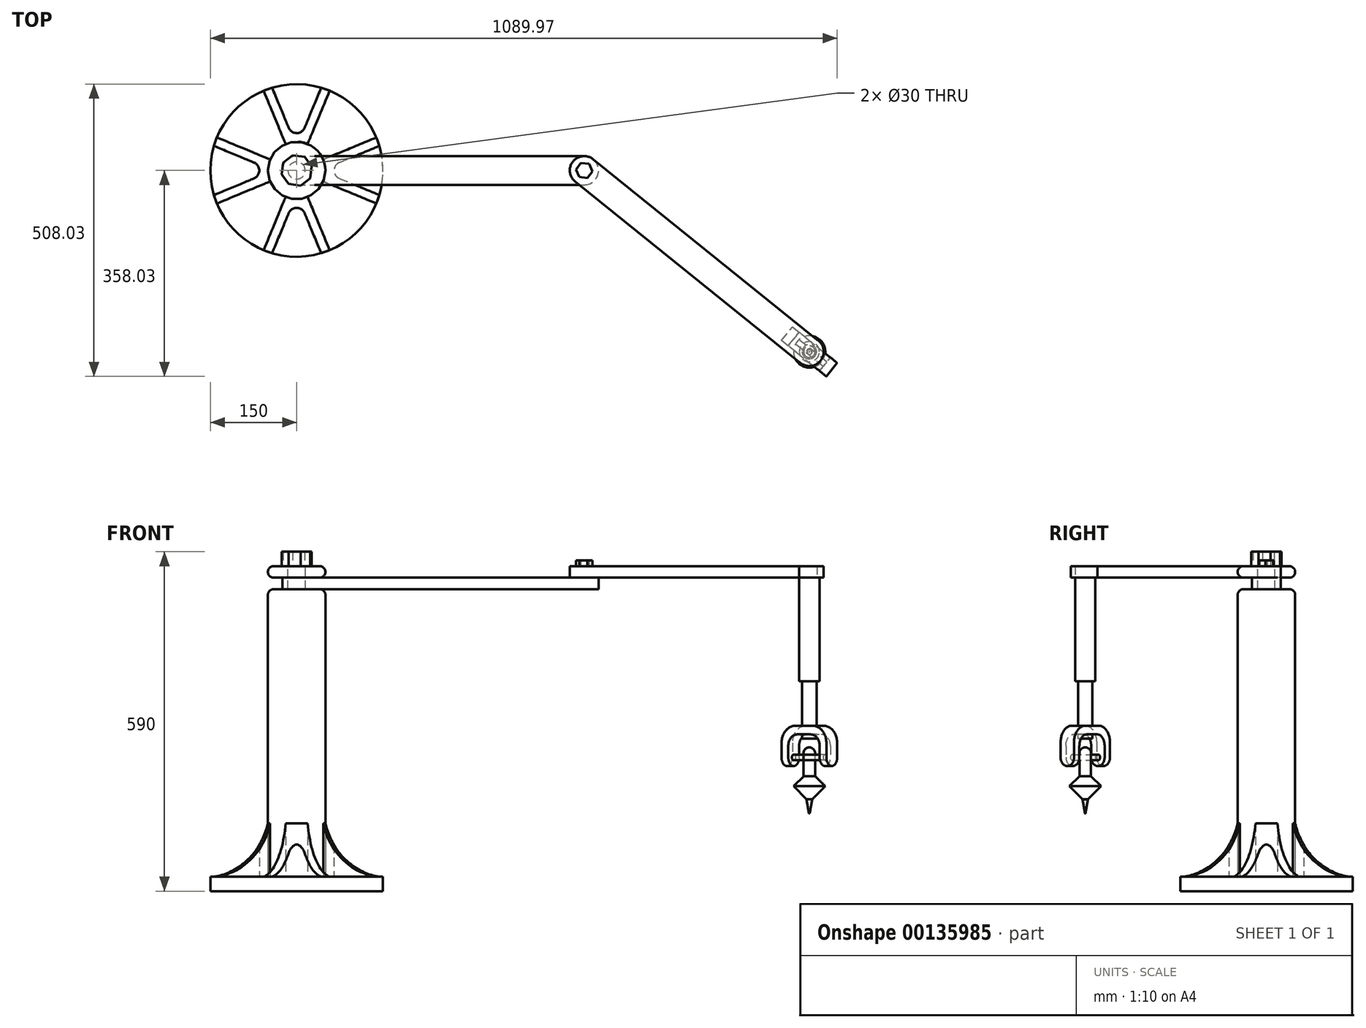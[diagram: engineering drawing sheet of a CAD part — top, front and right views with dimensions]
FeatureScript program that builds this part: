
annotation { "Feature Type Name" : "Feature", "Feature Type Description" : "" }
export const myFeature = defineFeature(function(context is Context, id is Id, definition is map)
    precondition{}
    {
        {
            var Q0;
            Q0=qCreatedBy(makeId("Top.planeOp"),FACE);
            var sketch = newSketch(context, id + "F0", { "sketchPlane" : qUnion([Q0])});
            skCircle(sketch, "E0", {"center": v(0, 0) * mm, "radius": 50 * mm});
            skSolve(sketch);
        }
        {
            var Q0;
            Q0 = qSketchRegion(id + "F0", true);
            extrude(context, id + "F1", {"entities" : qUnion([Q0]), "depth" : 500 * mm});
        }
        {
            var Q0;
            Q0=makeQuery(id+"F1.opExtrude","CAP_FACE",FACE,{"disambiguationData":[OSD([sQuery(id+"F0.wireOp",EDGE,"E0")])],"isStart":true});
            var sketch = newSketch(context, id + "F2", { "sketchPlane" : qUnion([Q0])});
            skCircle(sketch, "E1", {"center": v(0, 0) * mm, "radius": 150 * mm});
            skSolve(sketch);
        }
        {
            var Q0;
            Q0 = qSketchRegion(id + "F2", true);
            extrude(context, id + "F3", {"entities" : qUnion([Q0]), "operationType" : NewBodyOperationType.ADD, "depth" : 25 * mm});
        }
        {
            var Q0;
            Q0=qCreatedBy(makeId("Front.planeOp"),FACE);
            var sketch = newSketch(context, id + "F4", { "sketchPlane" : qUnion([Q0])});
            skLineSegment(sketch, "E2", {"start": v(50, 93.02) * mm, "end": v(50, 0) * mm});
            skPoint(sketch, "E3.orphan", {"position": v(-150, 0) * mm});
            skPoint(sketch, "E4.orphan", {"position": v(150, 0) * mm});
            skLineSegment(sketch, "E5", {"start": v(0, 0) * mm, "end": v(0, 181) * mm, "construction": true});
            skLineSegment(sketch, "E6.0", {"start": v(150, 0) * mm, "end": v(50, 0) * mm});
            skArc(sketch, "E7", {"start": v(50, 93.02) * mm, "mid": v(85.48, 30.9) * mm, "end": v(150, 0) * mm});
            skLineSegment(sketch, "E8.trimOffspring", {"start": v(0, 0) * mm, "end": v(-150, 0) * mm});
            skSolve(sketch);
        }
        {
            var Q0;
            Q0=makeQuery(id+"F4.imprint","IMPRINT",FACE,{"disambiguationData":[TD([[makeQuery(id+"F4.imprint","IMPRINT",EDGE,{"derivedFrom":sQuery(id+"F4.wireOp",EDGE,"E2")}),1.0]])]});
            var Q1;
            Q1=sQuery(id+"F4.wireOp",EDGE,"E5");
            revolve(context, id + "F5", {"entities" : qUnion([Q0]), "axis" : qUnion([Q1]), "revolveType" : RevolveType.SYMMETRIC, "angle" : 45 * degree});
        }
        {
            var Q0;
            Q0=makeQuery(id+"F3.opExtrude","CAP_FACE",FACE,{"disambiguationData":[OSD([sQuery(id+"F2.wireOp",EDGE,"E1")])],"isStart":true});
            var sketch = newSketch(context, id + "F6", { "sketchPlane" : qUnion([Q0])});
            skArc(sketch, "E9", {"start": v(74.26, 13.86) * mm, "mid": v(65, 0) * mm, "end": v(74.26, -13.86) * mm});
            skLineSegment(sketch, "E10", {"start": v(74.26, 13.86) * mm, "end": v(143.8, 42.66) * mm});
            skPoint(sketch, "E11.0.end.orphan", {"position": v(138.58, 57.4) * mm});
            skPoint(sketch, "E11.0.start.orphan", {"position": v(46.2, 19.13) * mm});
            skLineSegment(sketch, "E12.MirrorCS", {"start": v(74.26, -13.86) * mm, "end": v(143.8, -42.66) * mm});
            skArc(sketch, "E13.0", {"start": v(143.8, -42.66) * mm, "mid": v(150, 0) * mm, "end": v(143.8, 42.66) * mm});
            skPoint(sketch, "E14.orphan", {"position": v(63.73, 9.5) * mm});
            skPoint(sketch, "E15.orphan", {"position": v(63.73, -9.5) * mm});
            skPoint(sketch, "E16.orphan", {"position": v(156.25, 47.82) * mm});
            skPoint(sketch, "E17.orphan", {"position": v(156.25, -47.82) * mm});
            skSolve(sketch);
        }
        {
            var Q0;
            Q0 = qSketchRegion(id + "F6", true);
            extrude(context, id + "F7", {"entities" : qUnion([Q0]), "depth" : 70 * mm});
        }
        {
            var Q0;
            Q0=makeQuery(id+"F7.opExtrude","SWEPT_BODY",BODY,{"disambiguationData":[OSD([sQuery(id+"F6.wireOp",EDGE,"E9"),sQuery(id+"F6.wireOp",EDGE,"E10"),sQuery(id+"F6.wireOp",EDGE,"E12.MirrorCS"),sQuery(id+"F6.wireOp",EDGE,"E13.0")])]});
            var Q1;
            Q1=makeQuery(id+"F5.opRevolve","SWEPT_BODY",BODY,{"disambiguationData":[OSD([sQuery(id+"F4.wireOp",EDGE,"E2"),sQuery(id+"F4.wireOp",EDGE,"E6.0"),sQuery(id+"F4.wireOp",EDGE,"E7")])]});
            booleanBodies(context, id + "F8", {"operationType" : BooleanOperationType.SUBTRACTION, "tools" : qUnion([Q0]), "targets" : qUnion([Q1])});
        }
        {
            var Q0;
            Q0=makeQuery(id+"F5.opRevolve","SWEPT_BODY",BODY,{"disambiguationData":[OSD([sQuery(id+"F4.wireOp",EDGE,"E2"),sQuery(id+"F4.wireOp",EDGE,"E6.0"),sQuery(id+"F4.wireOp",EDGE,"E7")])]});
            var Q1;
            Q1=sQuery(id+"F4.wireOp",EDGE,"E5");
            circularPattern(context, id + "F9", {"entities" : qUnion([Q0]), "axis" : qUnion([Q1]), "angle" : 90 * degree, "instanceCount" : 4});
        }
        {
            var Q0;
            Q0=makeQuery(id+"F1.opExtrude","CAP_FACE",FACE,{"disambiguationData":[OSD([sQuery(id+"F0.wireOp",EDGE,"E0")])],"isStart":false});
            cPlane(context, id + "F10", {"entities" : qUnion([Q0]), "cplaneType" : CPlaneType.OFFSET, "offset" : 40 * mm, "width" : 150 * mm, "height" : 150 * mm});
        }
        {
            var Q0;
            Q0=qCreatedBy(id+"F10.planeOp",FACE);
            var sketch = newSketch(context, id + "F11", { "sketchPlane" : qUnion([Q0])});
            skCircle(sketch, "E18", {"center": v(0, 0) * mm, "radius": 50 * mm});
            skCircle(sketch, "E19", {"center": v(0, 0) * mm, "radius": 15 * mm});
            skSolve(sketch);
        }
        {
            var Q0;
            Q0 = qSketchRegion(id + "F11", true);
            var Q1;
            Q1=makeQuery(id+"F11.imprint","IMPRINT",FACE,{"disambiguationData":[TD([[makeQuery(id+"F11.imprint","IMPRINT",EDGE,{"derivedFrom":sQuery(id+"F11.wireOp",EDGE,"E18")}),1.0]])]});
            extrude(context, id + "F12", {"entities" : qUnion([Q0, Q1]), "oppositeDirection" : true, "depth" : 20 * mm});
        }
        {
            var Q0;
            Q0=makeQuery(id+"F1.opExtrude","CAP_FACE",FACE,{"disambiguationData":[OSD([sQuery(id+"F0.wireOp",EDGE,"E0")])],"isStart":false});
            var sketch = newSketch(context, id + "F13", { "sketchPlane" : qUnion([Q0])});
            skLineSegment(sketch, "E20.bottom", {"start": v(0, 25) * mm, "end": v(500, 25) * mm});
            skLineSegment(sketch, "E20.top", {"start": v(0, -25) * mm, "end": v(500, -25) * mm});
            skArc(sketch, "E21", {"start": v(0, 25) * mm, "mid": v(-25, 0) * mm, "end": v(0, -25) * mm});
            skArc(sketch, "E22", {"start": v(500, -25) * mm, "mid": v(525, 0) * mm, "end": v(500, 25) * mm});
            skSolve(sketch);
        }
        {
            var Q0;
            Q0 = qSketchRegion(id + "F13", true);
            var Q1;
            {var subQ0=sQuery(id+"F13.wireOp",EDGE,"E22");Q1=makeQuery(id+"F13.imprint","IMPRINT",FACE,{"disambiguationData":[TD([[makeQuery(id+"F13.imprint","IMPRINT",EDGE,{"derivedFrom":subQ0}),1.0]])]});}
            extrude(context, id + "F14", {"entities" : qUnion([Q0, Q1]), "depth" : 20 * mm});
        }
        {
            var Q0;
            Q0=makeQuery(id+"F14.opExtrude","CAP_FACE",FACE,{"disambiguationData":[OSD([sQuery(id+"F13.wireOp",EDGE,"E20.bottom"),sQuery(id+"F13.wireOp",EDGE,"E20.top"),sQuery(id+"F13.wireOp",EDGE,"E21"),sQuery(id+"F13.wireOp",EDGE,"E22")])],"isStart":false});
            var sketch = newSketch(context, id + "F15", { "sketchPlane" : qUnion([Q0])});
            skCircle(sketch, "E23.0", {"center": v(0, 0) * mm, "radius": 15 * mm});
            skSolve(sketch);
        }
        {
            var Q0;
            Q0 = qSketchRegion(id + "F15", true);
            extrude(context, id + "F16", {"entities" : qUnion([Q0]), "oppositeDirection" : true, "depth" : 20 * mm});
        }
        {
            var Q0;
            Q0=makeQuery(id+"F16.opExtrude","SWEPT_BODY",BODY,{"disambiguationData":[OSD([sQuery(id+"F15.wireOp",EDGE,"E23.0")])]});
            var Q1;
            Q1=makeQuery(id+"F14.opExtrude","SWEPT_BODY",BODY,{"disambiguationData":[OSD([sQuery(id+"F13.wireOp",EDGE,"E20.bottom"),sQuery(id+"F13.wireOp",EDGE,"E20.top"),sQuery(id+"F13.wireOp",EDGE,"E21"),sQuery(id+"F13.wireOp",EDGE,"E22")])]});
            booleanBodies(context, id + "F17", {"operationType" : BooleanOperationType.SUBTRACTION, "tools" : qUnion([Q0]), "targets" : qUnion([Q1])});
        }
        {
            var Q0;
            Q0=makeQuery(id+"F12.opExtrude","CAP_FACE",FACE,{"disambiguationData":[OSD([sQuery(id+"F11.wireOp",EDGE,"E18"),sQuery(id+"F11.wireOp",EDGE,"E19")])],"isStart":true});
            var sketch = newSketch(context, id + "F18", { "sketchPlane" : qUnion([Q0])});
            skCircle(sketch, "E24.0", {"center": v(0, 0) * mm, "radius": 15 * mm});
            skSolve(sketch);
        }
        {
            var Q0;
            Q0 = qSketchRegion(id + "F18", true);
            extrude(context, id + "F19", {"entities" : qUnion([Q0]), "oppositeDirection" : true, "depth" : 40 * mm});
        }
        {
            var Q0;
            Q0=makeQuery(id+"F19.opExtrude","CAP_FACE",FACE,{"disambiguationData":[OSD([sQuery(id+"F18.wireOp",EDGE,"E24.0")])],"isStart":true});
            var sketch = newSketch(context, id + "F20", { "sketchPlane" : qUnion([Q0])});
            skCircle(sketch, "E25.cCircle", {"center": v(0, 0) * mm, "radius": 27.24 * mm, "construction": true});
            skLineSegment(sketch, "E25.0", {"start": v(23.56, -13.68) * mm, "end": v(6.98, -26.33) * mm});
            skLineSegment(sketch, "E25.1", {"start": v(6.98, -26.33) * mm, "end": v(-13.68, -23.56) * mm});
            skLineSegment(sketch, "E25.2", {"start": v(-13.68, -23.56) * mm, "end": v(-26.33, -6.98) * mm});
            skLineSegment(sketch, "E25.3", {"start": v(-26.33, -6.98) * mm, "end": v(-23.56, 13.68) * mm});
            skLineSegment(sketch, "E25.4", {"start": v(-23.56, 13.68) * mm, "end": v(-6.98, 26.33) * mm});
            skLineSegment(sketch, "E25.5", {"start": v(-6.98, 26.33) * mm, "end": v(13.68, 23.56) * mm});
            skLineSegment(sketch, "E25.6", {"start": v(13.68, 23.56) * mm, "end": v(26.33, 6.98) * mm});
            skLineSegment(sketch, "E25.7", {"start": v(26.33, 6.98) * mm, "end": v(23.56, -13.68) * mm});
            skSolve(sketch);
        }
        {
            var Q0;
            Q0 = qSketchRegion(id + "F20", true);
            extrude(context, id + "F21", {"entities" : qUnion([Q0]), "depth" : 25 * mm});
        }
        {
            var Q0;
            Q0=makeQuery(id+"F14.opExtrude","CAP_FACE",FACE,{"disambiguationData":[OSD([sQuery(id+"F13.wireOp",EDGE,"E20.bottom"),sQuery(id+"F13.wireOp",EDGE,"E20.top"),sQuery(id+"F13.wireOp",EDGE,"E21"),sQuery(id+"F13.wireOp",EDGE,"E22")])],"isStart":false});
            var sketch = newSketch(context, id + "F22", { "sketchPlane" : qUnion([Q0])});
            skArc(sketch, "E26", {"start": v(515.68, 19.47) * mm, "mid": v(480.52, 15.67) * mm, "end": v(484.33, -19.48) * mm});
            skLineSegment(sketch, "E27", {"start": v(484.33, -19.48) * mm, "end": v(873.93, -332.87) * mm});
            skLineSegment(sketch, "E28", {"start": v(515.68, 19.47) * mm, "end": v(905.11, -294.13) * mm});
            skPoint(sketch, "E29.orphan", {"position": v(500, 32.1) * mm});
            skArc(sketch, "E30", {"start": v(873.93, -332.87) * mm, "mid": v(911, -330.79) * mm, "end": v(905.11, -294.13) * mm});
            skSolve(sketch);
        }
        {
            var Q0;
            Q0 = qSketchRegion(id + "F22", true);
            extrude(context, id + "F23", {"entities" : qUnion([Q0]), "operationType" : NewBodyOperationType.ADD, "depth" : 20 * mm});
        }
        {
            var Q0;
            Q0=makeQuery(id+"F23.opExtrude","CAP_FACE",FACE,{"disambiguationData":[OSD([sQuery(id+"F22.wireOp",EDGE,"E26"),sQuery(id+"F22.wireOp",EDGE,"E27"),sQuery(id+"F22.wireOp",EDGE,"E28"),sQuery(id+"F22.wireOp",EDGE,"E30")])],"isStart":false});
            var sketch = newSketch(context, id + "F24", { "sketchPlane" : qUnion([Q0])});
            skCircle(sketch, "E31.cCircle", {"center": v(500, 0) * mm, "radius": 12.27 * mm, "construction": true});
            skLineSegment(sketch, "E31.0", {"start": v(514.08, -1.6) * mm, "end": v(505.65, -13) * mm});
            skLineSegment(sketch, "E31.1", {"start": v(505.65, -13) * mm, "end": v(491.57, -11.39) * mm});
            skLineSegment(sketch, "E31.2", {"start": v(491.57, -11.39) * mm, "end": v(485.92, 1.6) * mm});
            skLineSegment(sketch, "E31.3", {"start": v(485.92, 1.6) * mm, "end": v(494.35, 13) * mm});
            skLineSegment(sketch, "E31.4", {"start": v(494.35, 13) * mm, "end": v(508.43, 11.39) * mm});
            skLineSegment(sketch, "E31.5", {"start": v(508.43, 11.39) * mm, "end": v(514.08, -1.6) * mm});
            skPoint(sketch, "E31.0.midPoint", {"position": v(509.86, -7.3) * mm});
            skSolve(sketch);
        }
        {
            var Q0;
            Q0 = qSketchRegion(id + "F24", true);
            extrude(context, id + "F25", {"entities" : qUnion([Q0]), "operationType" : NewBodyOperationType.ADD, "depth" : 10 * mm});
        }
        {
            var Q0;
            Q0=makeQuery(id+"F23.opExtrude","CAP_FACE",FACE,{"disambiguationData":[OSD([sQuery(id+"F22.wireOp",EDGE,"E26"),sQuery(id+"F22.wireOp",EDGE,"E27"),sQuery(id+"F22.wireOp",EDGE,"E28"),sQuery(id+"F22.wireOp",EDGE,"E30")])],"isStart":false});
            var sketch = newSketch(context, id + "F26", { "sketchPlane" : qUnion([Q0])});
            skCircle(sketch, "E32", {"center": v(891.52, -315.11) * mm, "radius": 17.5 * mm});
            skSolve(sketch);
        }
        {
            var Q0;
            Q0 = qSketchRegion(id + "F26", true);
            extrude(context, id + "F27", {"entities" : qUnion([Q0]), "operationType" : NewBodyOperationType.REMOVE, "oppositeDirection" : true, "depth" : 25 * mm});
        }
        {
            var Q0;
            Q0=makeQuery(id+"F23.opExtrude","CAP_FACE",FACE,{"disambiguationData":[OSD([sQuery(id+"F22.wireOp",EDGE,"E26"),sQuery(id+"F22.wireOp",EDGE,"E27"),sQuery(id+"F22.wireOp",EDGE,"E28"),sQuery(id+"F22.wireOp",EDGE,"E30")])],"isStart":false});
            var sketch = newSketch(context, id + "F28", { "sketchPlane" : qUnion([Q0])});
            skCircle(sketch, "E33.0", {"center": v(891.52, -315.11) * mm, "radius": 17.5 * mm});
            skSolve(sketch);
        }
        {
            var Q0;
            Q0 = qSketchRegion(id + "F28", true);
            extrude(context, id + "F29", {"entities" : qUnion([Q0]), "operationType" : NewBodyOperationType.ADD, "oppositeDirection" : true, "depth" : 200 * mm});
        }
        {
            var Q0;
            Q0=makeQuery(id+"F29.opExtrude","CAP_FACE",FACE,{"disambiguationData":[OSD([sQuery(id+"F28.wireOp",EDGE,"E33.0")])],"isStart":false});
            var sketch = newSketch(context, id + "F30", { "sketchPlane" : qUnion([Q0])});
            skCircle(sketch, "E34", {"center": v(891.52, 315.11) * mm, "radius": 12.5 * mm});
            skSolve(sketch);
        }
        {
            var Q0;
            Q0 = qSketchRegion(id + "F30", true);
            extrude(context, id + "F31", {"entities" : qUnion([Q0]), "operationType" : NewBodyOperationType.ADD, "depth" : 100 * mm});
        }
        {
            var Q0;
            Q0=makeQuery(id+"F23.opExtrude","CAP_EDGE",EDGE,{"disambiguationData":[OSD([sQuery(id+"F22.wireOp",EDGE,"E30")])],"isStart":false});
            cPlane(context, id + "F32", {"entities" : qUnion([Q0]), "cplaneType" : CPlaneType.LINE_ANGLE, "offset" : 25 * mm, "angle" : 141 * degree, "width" : 150 * mm, "height" : 150 * mm});
        }
        {
            var Q0;
            Q0=makeQuery(id+"F23.opExtrude","SWEPT_FACE",FACE,{"disambiguationData":[OSD([sQuery(id+"F22.wireOp",EDGE,"E27")])]});
            cPlane(context, id + "F33", {"entities" : qUnion([Q0]), "cplaneType" : CPlaneType.OFFSET, "offset" : 25 * mm, "oppositeDirection" : true, "width" : 150 * mm, "height" : 150 * mm});
        }
        {
            var Q0;
            Q0=qCreatedBy(id+"F33.planeOp",FACE);
            var sketch = newSketch(context, id + "F34", { "sketchPlane" : qUnion([Q0])});
            skLineSegment(sketch, "E35", {"start": v(842.18, 262.5) * mm, "end": v(942.18, 262.5) * mm});
            skLineSegment(sketch, "E36", {"start": v(857.18, 247.5) * mm, "end": v(927.18, 247.5) * mm});
            skLineSegment(sketch, "E37", {"start": v(842.18, 262.5) * mm, "end": v(842.18, 192.5) * mm});
            skLineSegment(sketch, "E38", {"start": v(942.18, 262.5) * mm, "end": v(942.18, 192.5) * mm});
            skLineSegment(sketch, "E39", {"start": v(842.18, 192.5) * mm, "end": v(857.18, 192.5) * mm});
            skLineSegment(sketch, "E40", {"start": v(857.18, 192.5) * mm, "end": v(857.18, 247.5) * mm});
            skLineSegment(sketch, "E41", {"start": v(927.18, 247.5) * mm, "end": v(927.18, 192.5) * mm});
            skLineSegment(sketch, "E42", {"start": v(927.18, 192.5) * mm, "end": v(942.18, 192.5) * mm});
            skSolve(sketch);
        }
        {
            var Q0;
            Q0 = qSketchRegion(id + "F34", true);
            extrude(context, id + "F35", {"entities" : qUnion([Q0]), "operationType" : NewBodyOperationType.ADD, "endBound" : BoundingType.SYMMETRIC, "depth" : 30 * mm});
        }
        {
            var Q0;
            Q0=makeQuery(id+"F35.opExtrude","SWEPT_EDGE",EDGE,{"disambiguationData":[OSD([sQuery(id+"F34.wireOp",EDGE,"E35"),sQuery(id+"F34.wireOp",EDGE,"E38")])]});
            var Q1;
            Q1=makeQuery(id+"F35.opExtrude","SWEPT_EDGE",EDGE,{"disambiguationData":[OSD([sQuery(id+"F34.wireOp",EDGE,"E35"),sQuery(id+"F34.wireOp",EDGE,"E37")])]});
            fillet(context, id + "F36", {"entities" : qUnion([Q0, Q1]), "radius" : 30 * mm, "tangentPropagation" : true, "allowEdgeOverflow" : false});
        }
        {
            var Q0;
            Q0=makeQuery(id+"F35.opExtrude","SWEPT_EDGE",EDGE,{"disambiguationData":[OSD([sQuery(id+"F34.wireOp",EDGE,"E36"),sQuery(id+"F34.wireOp",EDGE,"E40")])]});
            var Q1;
            Q1=makeQuery(id+"F35.opExtrude","SWEPT_EDGE",EDGE,{"disambiguationData":[OSD([sQuery(id+"F34.wireOp",EDGE,"E36"),sQuery(id+"F34.wireOp",EDGE,"E41")])]});
            fillet(context, id + "F37", {"entities" : qUnion([Q0, Q1]), "radius" : 20 * mm, "tangentPropagation" : true, "allowEdgeOverflow" : false});
        }
        {
            var Q0;
            Q0=makeQuery(id+"F35.opExtrude","CAP_EDGE",EDGE,{"disambiguationData":[OSD([sQuery(id+"F34.wireOp",EDGE,"E42")])],"isStart":false});
            var Q1;
            Q1=makeQuery(id+"F35.opExtrude","CAP_EDGE",EDGE,{"disambiguationData":[OSD([sQuery(id+"F34.wireOp",EDGE,"E39")])],"isStart":false});
            var Q2;
            Q2=makeQuery(id+"F35.opExtrude","CAP_EDGE",EDGE,{"disambiguationData":[OSD([sQuery(id+"F34.wireOp",EDGE,"E42")])],"isStart":true});
            var Q3;
            Q3=makeQuery(id+"F35.opExtrude","CAP_EDGE",EDGE,{"disambiguationData":[OSD([sQuery(id+"F34.wireOp",EDGE,"E39")])],"isStart":true});
            fillet(context, id + "F38", {"entities" : qUnion([Q0, Q1, Q2, Q3]), "radius" : 15 * mm, "tangentPropagation" : true, "allowEdgeOverflow" : false});
        }
        {
            var Q0;
            Q0=makeQuery(id+"F35.opExtrude","SWEPT_FACE",FACE,{"disambiguationData":[OSD([sQuery(id+"F34.wireOp",EDGE,"E40")])]});
            var sketch = newSketch(context, id + "F39", { "sketchPlane" : qUnion([Q0])});
            skCircle(sketch, "E43", {"center": v(313.4, 207.5) * mm, "radius": 5 * mm});
            skSolve(sketch);
        }
        {
            var Q0;
            Q0 = qSketchRegion(id + "F39", true);
            extrude(context, id + "F40", {"entities" : qUnion([Q0]), "operationType" : NewBodyOperationType.ADD, "endBound" : BoundingType.UP_TO_NEXT, "depth" : 25 * mm});
        }
        {
            var Q0;
            Q0=makeQuery(id+"F31.opExtrude","CAP_FACE",FACE,{"disambiguationData":[OSD([sQuery(id+"F30.wireOp",EDGE,"E34")])],"isStart":false});
            cPlane(context, id + "F41", {"entities" : qUnion([Q0]), "cplaneType" : CPlaneType.OFFSET, "offset" : 15 * mm, "width" : 150 * mm, "height" : 150 * mm});
        }
        {
            var Q0;
            Q0=qCreatedBy(id+"F41.planeOp",FACE);
            var sketch = newSketch(context, id + "F42", { "sketchPlane" : qUnion([Q0])});
            skArc(sketch, "E44.0", {"start": v(873.93, 332.87) * mm, "mid": v(911, 330.79) * mm, "end": v(905.11, 294.13) * mm});
            skCircle(sketch, "E45", {"center": v(891.52, 315.11) * mm, "radius": 10 * mm});
            skSolve(sketch);
        }
        {
            var Q0;
            Q0 = qSketchRegion(id + "F42", true);
            extrude(context, id + "F43", {"entities" : qUnion([Q0]), "depth" : 50 * mm});
        }
        {
            var Q0;
            Q0=makeQuery(id+"F43.opExtrude","CAP_EDGE",EDGE,{"disambiguationData":[OSD([sQuery(id+"F42.wireOp",EDGE,"E45")])],"isStart":true});
            fillet(context, id + "F44", {"entities" : qUnion([Q0]), "radius" : 10 * mm, "tangentPropagation" : true, "allowEdgeOverflow" : false});
        }
        {
            var Q0;
            Q0=qCreatedBy(id+"F33.planeOp",FACE);
            var sketch = newSketch(context, id + "F45", { "sketchPlane" : qUnion([Q0])});
            skLineSegment(sketch, "E46.0", {"start": v(902.18, 175) * mm, "end": v(892.26, 175) * mm});
            skLineSegment(sketch, "E47", {"start": v(902.18, 175) * mm, "end": v(919.85, 157.32) * mm});
            skLineSegment(sketch, "E48", {"start": v(919.85, 157.32) * mm, "end": v(897.18, 134.64) * mm});
            skLineSegment(sketch, "E49", {"start": v(892.26, 195.42) * mm, "end": v(892.26, 133.02) * mm, "construction": true});
            skPoint(sketch, "E50.orphan", {"position": v(882.18, 175) * mm});
            skLineSegment(sketch, "E51", {"start": v(897.18, 134.64) * mm, "end": v(892.26, 134.64) * mm});
            skLineSegment(sketch, "E52", {"start": v(892.26, 134.64) * mm, "end": v(892.26, 175) * mm});
            skSolve(sketch);
        }
        {
            var Q0;
            Q0 = qSketchRegion(id + "F45", true);
            var Q1;
            Q1=sQuery(id+"F45.wireOp",EDGE,"E49");
            revolve(context, id + "F46", {"entities" : qUnion([Q0]), "axis" : qUnion([Q1]), "revolveType" : RevolveType.FULL});
        }
        {
            var Q0;
            Q0=qCreatedBy(id+"F33.planeOp",FACE);
            var sketch = newSketch(context, id + "F47", { "sketchPlane" : qUnion([Q0])});
            skLineSegment(sketch, "E53.0", {"start": v(892.26, 134.64) * mm, "end": v(897.18, 134.64) * mm});
            skLineSegment(sketch, "E54", {"start": v(892.26, 153.07) * mm, "end": v(892.26, 106.7) * mm, "construction": true});
            skLineSegment(sketch, "E55", {"start": v(897.18, 134.64) * mm, "end": v(892.84, 110.02) * mm});
            skPoint(sketch, "E56.orphan", {"position": v(887.34, 134.64) * mm});
            skLineSegment(sketch, "E57", {"start": v(892.26, 134.64) * mm, "end": v(892.26, 110.02) * mm});
            skLineSegment(sketch, "E58", {"start": v(892.26, 110.02) * mm, "end": v(892.84, 110.02) * mm});
            skSolve(sketch);
        }
        {
            var Q0;
            Q0 = qSketchRegion(id + "F47", true);
            var Q1;
            Q1=sQuery(id+"F47.wireOp",EDGE,"E54");
            revolve(context, id + "F48", {"entities" : qUnion([Q0]), "axis" : qUnion([Q1]), "revolveType" : RevolveType.FULL});
        }
        {
            var Q0;
            Q0=makeQuery(id+"F48.opRevolve","SWEPT_FACE",FACE,{"disambiguationData":[OSD([sQuery(id+"F47.wireOp",EDGE,"E58")])]});
            shell(context, id + "F49", {"entities" : qUnion([Q0]), "thickness" : .9 * mm});
        }
        {
            var Q0;
            Q0=makeQuery(id+"F12.opExtrude","CAP_EDGE",EDGE,{"disambiguationData":[OSD([sQuery(id+"F11.wireOp",EDGE,"E18")])],"isStart":false});
            var Q1;
            Q1=makeQuery(id+"F12.opExtrude","CAP_EDGE",EDGE,{"disambiguationData":[OSD([sQuery(id+"F11.wireOp",EDGE,"E18")])],"isStart":true});
            var Q2;
            Q2=makeQuery(id+"F1.opExtrude","CAP_EDGE",EDGE,{"disambiguationData":[OSD([sQuery(id+"F0.wireOp",EDGE,"E0")])],"isStart":false});
            fillet(context, id + "F50", {"entities" : qUnion([Q0, Q1, Q2]), "radius" : 10 * mm, "tangentPropagation" : true, "allowEdgeOverflow" : false});
        }
    });
